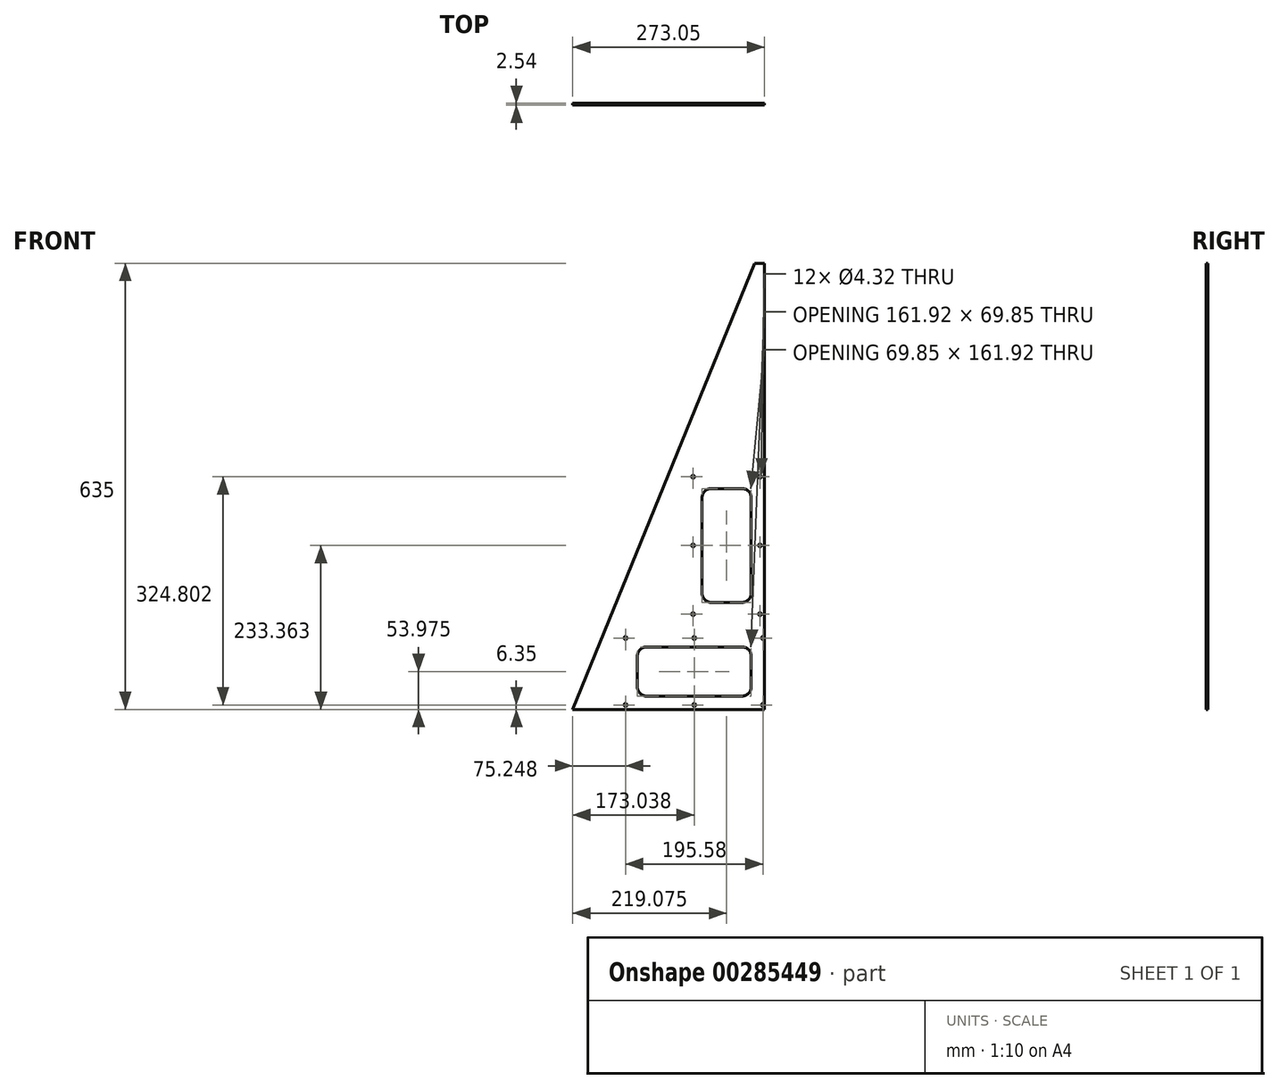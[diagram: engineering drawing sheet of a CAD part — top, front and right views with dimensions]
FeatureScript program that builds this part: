
annotation { "Feature Type Name" : "Feature", "Feature Type Description" : "" }
export const myFeature = defineFeature(function(context is Context, id is Id, definition is map)
    precondition{}
    {
        {
            var Q0;
            Q0=qCreatedBy(makeId("Front.planeOp"),FACE);
            var sketch = newSketch(context, id + "F0", { "sketchPlane" : qUnion([Q0])});
            skLineSegment(sketch, "E0", {"start": v(0, 0) * mm, "end": v(0, 635) * mm});
            skArc(sketch, "E1.MirrorCS", {"start": v(-88.9, 165.1) * mm, "mid": v(-85.18, 156.12) * mm, "end": v(-76.2, 152.4) * mm});
            skArc(sketch, "E2.MirrorCS", {"start": v(-76.2, 314.33) * mm, "mid": v(-85.18, 310.6) * mm, "end": v(-88.9, 301.63) * mm});
            skArc(sketch, "E3.MirrorCS", {"start": v(-180.97, 31.75) * mm, "mid": v(-177.26, 22.77) * mm, "end": v(-168.28, 19.05) * mm});
            skArc(sketch, "E4.MirrorCS", {"start": v(-19.05, 301.63) * mm, "mid": v(-22.77, 310.6) * mm, "end": v(-31.75, 314.33) * mm});
            skArc(sketch, "E5.MirrorCS", {"start": v(-31.75, 152.4) * mm, "mid": v(-22.77, 156.12) * mm, "end": v(-19.05, 165.1) * mm});
            skArc(sketch, "E6.MirrorCS", {"start": v(-19.05, 76.2) * mm, "mid": v(-22.77, 85.18) * mm, "end": v(-31.75, 88.9) * mm});
            skArc(sketch, "E7.MirrorCS", {"start": v(-168.28, 88.9) * mm, "mid": v(-177.26, 85.18) * mm, "end": v(-180.97, 76.2) * mm});
            skArc(sketch, "E8.MirrorCS", {"start": v(-31.75, 19.05) * mm, "mid": v(-22.77, 22.77) * mm, "end": v(-19.05, 31.75) * mm});
            skLineSegment(sketch, "E9.MirrorCS", {"start": v(-88.9, 165.1) * mm, "end": v(-88.9, 301.63) * mm});
            skLineSegment(sketch, "E10.MirrorCS", {"start": v(-76.2, 314.33) * mm, "end": v(-31.75, 314.33) * mm});
            skLineSegment(sketch, "E11.MirrorCS", {"start": v(-14.02, 635) * mm, "end": v(-273.05, 0) * mm});
            skLineSegment(sketch, "E12.MirrorCS", {"start": v(-168.28, 88.9) * mm, "end": v(-31.75, 88.9) * mm});
            skLineSegment(sketch, "E13.MirrorCS", {"start": v(-180.97, 76.2) * mm, "end": v(-180.97, 31.75) * mm});
            skLineSegment(sketch, "E14.MirrorCS", {"start": v(-76.2, 152.4) * mm, "end": v(-31.75, 152.4) * mm});
            skLineSegment(sketch, "E15.MirrorCS", {"start": v(-168.28, 19.05) * mm, "end": v(-31.75, 19.05) * mm});
            skLineSegment(sketch, "E16.MirrorCS", {"start": v(-19.05, 76.2) * mm, "end": v(-19.05, 31.75) * mm});
            skLineSegment(sketch, "E17.MirrorCS", {"start": v(-19.05, 165.1) * mm, "end": v(-19.05, 301.63) * mm});
            skLineSegment(sketch, "E18", {"start": v(-14.02, 635) * mm, "end": v(0, 635) * mm});
            skLineSegment(sketch, "E19", {"start": v(0, 0) * mm, "end": v(-273.05, 0) * mm});
            skSolve(sketch);
        }
        {
            var Q0;
            Q0=qSketchRegion(id+"F0",true);
            extrude(context, id + "F1", {"entities" : qUnion([Q0]), "depth" : 2.54 * mm});
        }
        {
            var Q0;
            Q0=makeQuery(id+"F1.opExtrude","CAP_FACE",FACE,{"disambiguationData":[OSD([sQuery(id+"F0.wireOp",EDGE,"E0"),sQuery(id+"F0.wireOp",EDGE,"de29adb0-a0ae-424e-9d03-0ac620758d970.MirrorCS"),sQuery(id+"F0.wireOp",EDGE,"de29adb0-a0ae-424e-9d03-0ac620758d971.MirrorCS"),sQuery(id+"F0.wireOp",EDGE,"de29adb0-a0ae-424e-9d03-0ac620758d972.MirrorCS"),sQuery(id+"F0.wireOp",EDGE,"de29adb0-a0ae-424e-9d03-0ac620758d973.MirrorCS"),sQuery(id+"F0.wireOp",EDGE,"de29adb0-a0ae-424e-9d03-0ac620758d974.MirrorCS"),sQuery(id+"F0.wireOp",EDGE,"de29adb0-a0ae-424e-9d03-0ac620758d975.MirrorCS"),sQuery(id+"F0.wireOp",EDGE,"de29adb0-a0ae-424e-9d03-0ac620758d976.MirrorCS"),sQuery(id+"F0.wireOp",EDGE,"de29adb0-a0ae-424e-9d03-0ac620758d977.MirrorCS"),sQuery(id+"F0.wireOp",EDGE,"de29adb0-a0ae-424e-9d03-0ac620758d978.MirrorCS"),sQuery(id+"F0.wireOp",EDGE,"de29adb0-a0ae-424e-9d03-0ac620758d979.MirrorCS"),sQuery(id+"F0.wireOp",EDGE,"de29adb0-a0ae-424e-9d03-0ac620758d9711.MirrorCS"),sQuery(id+"F0.wireOp",EDGE,"de29adb0-a0ae-424e-9d03-0ac620758d9715.MirrorCS"),sQuery(id+"F0.wireOp",EDGE,"de29adb0-a0ae-424e-9d03-0ac620758d9716.MirrorCS"),sQuery(id+"F0.wireOp",EDGE,"de29adb0-a0ae-424e-9d03-0ac620758d9717.MirrorCS"),sQuery(id+"F0.wireOp",EDGE,"de29adb0-a0ae-424e-9d03-0ac620758d9718.MirrorCS"),sQuery(id+"F0.wireOp",EDGE,"de29adb0-a0ae-424e-9d03-0ac620758d9719.MirrorCS"),sQuery(id+"F0.wireOp",EDGE,"de29adb0-a0ae-424e-9d03-0ac620758d9721.MirrorCS"),sQuery(id+"F0.wireOp",EDGE,"de29adb0-a0ae-424e-9d03-0ac620758d9723.MirrorCS"),sQuery(id+"F0.wireOp",EDGE,"de29adb0-a0ae-424e-9d03-0ac620758d9725.MirrorCS")])],"isStart":false});
            var sketch = newSketch(context, id + "F2", { "sketchPlane" : qUnion([Q0])});
            skPoint(sketch, "E20", {"position": v(-197.8, 101.6) * mm});
            skPoint(sketch, "E21", {"position": v(-100.01, 101.6) * mm});
            skPoint(sketch, "E22", {"position": v(-2.22, 101.6) * mm});
            skPoint(sketch, "E23", {"position": v(-2.22, 6.35) * mm});
            skPoint(sketch, "E24", {"position": v(-100.01, 6.35) * mm});
            skPoint(sketch, "E25", {"position": v(-197.8, 6.35) * mm});
            skLineSegment(sketch, "E26", {"start": v(-100.01, 88.9) * mm, "end": v(-100.01, 6.35) * mm, "construction": true});
            skPoint(sketch, "E27", {"position": v(-101.6, 135.57) * mm});
            skPoint(sketch, "E28", {"position": v(-101.6, 233.36) * mm});
            skPoint(sketch, "E29", {"position": v(-101.6, 331.15) * mm});
            skPoint(sketch, "E30", {"position": v(-6.35, 331.15) * mm});
            skPoint(sketch, "E31", {"position": v(-6.35, 233.36) * mm});
            skPoint(sketch, "E32", {"position": v(-6.35, 135.57) * mm});
            skLineSegment(sketch, "E33", {"start": v(-88.9, 233.36) * mm, "end": v(-6.35, 233.36) * mm, "construction": true});
            skPoint(sketch, "E33.endSnap0", {"position": v(-19.05, 233.36) * mm});
            skSolve(sketch);
        }
        {
            var Q0;
            Q0=sQuery(id+"F2.wireOp",VERTEX,"E29");
            var Q1;
            Q1=sQuery(id+"F2.wireOp",VERTEX,"E30");
            var Q2;
            Q2=sQuery(id+"F2.wireOp",VERTEX,"E31");
            var Q3;
            Q3=sQuery(id+"F2.wireOp",VERTEX,"E28");
            var Q4;
            Q4=sQuery(id+"F2.wireOp",VERTEX,"E27");
            var Q5;
            Q5=sQuery(id+"F2.wireOp",VERTEX,"E32");
            var Q6;
            Q6=sQuery(id+"F2.wireOp",VERTEX,"E20");
            var Q7;
            Q7=sQuery(id+"F2.wireOp",VERTEX,"E25");
            var Q8;
            Q8=sQuery(id+"F2.wireOp",VERTEX,"E24");
            var Q9;
            Q9=sQuery(id+"F2.wireOp",VERTEX,"E21");
            var Q10;
            Q10=sQuery(id+"F2.wireOp",VERTEX,"E22");
            var Q11;
            Q11=sQuery(id+"F2.wireOp",VERTEX,"E23");
            var Q12;
            Q12=makeQuery(id+"F1.opExtrude","SWEPT_BODY",BODY,{"disambiguationData":[OSD([sQuery(id+"F0.wireOp",EDGE,"E0"),sQuery(id+"F0.wireOp",EDGE,"de29adb0-a0ae-424e-9d03-0ac620758d970.MirrorCS"),sQuery(id+"F0.wireOp",EDGE,"de29adb0-a0ae-424e-9d03-0ac620758d971.MirrorCS"),sQuery(id+"F0.wireOp",EDGE,"de29adb0-a0ae-424e-9d03-0ac620758d972.MirrorCS"),sQuery(id+"F0.wireOp",EDGE,"de29adb0-a0ae-424e-9d03-0ac620758d973.MirrorCS"),sQuery(id+"F0.wireOp",EDGE,"de29adb0-a0ae-424e-9d03-0ac620758d974.MirrorCS"),sQuery(id+"F0.wireOp",EDGE,"de29adb0-a0ae-424e-9d03-0ac620758d975.MirrorCS"),sQuery(id+"F0.wireOp",EDGE,"de29adb0-a0ae-424e-9d03-0ac620758d976.MirrorCS"),sQuery(id+"F0.wireOp",EDGE,"de29adb0-a0ae-424e-9d03-0ac620758d977.MirrorCS"),sQuery(id+"F0.wireOp",EDGE,"de29adb0-a0ae-424e-9d03-0ac620758d978.MirrorCS"),sQuery(id+"F0.wireOp",EDGE,"de29adb0-a0ae-424e-9d03-0ac620758d979.MirrorCS"),sQuery(id+"F0.wireOp",EDGE,"de29adb0-a0ae-424e-9d03-0ac620758d9711.MirrorCS"),sQuery(id+"F0.wireOp",EDGE,"de29adb0-a0ae-424e-9d03-0ac620758d9715.MirrorCS"),sQuery(id+"F0.wireOp",EDGE,"de29adb0-a0ae-424e-9d03-0ac620758d9716.MirrorCS"),sQuery(id+"F0.wireOp",EDGE,"de29adb0-a0ae-424e-9d03-0ac620758d9717.MirrorCS"),sQuery(id+"F0.wireOp",EDGE,"de29adb0-a0ae-424e-9d03-0ac620758d9718.MirrorCS"),sQuery(id+"F0.wireOp",EDGE,"de29adb0-a0ae-424e-9d03-0ac620758d9719.MirrorCS"),sQuery(id+"F0.wireOp",EDGE,"de29adb0-a0ae-424e-9d03-0ac620758d9721.MirrorCS"),sQuery(id+"F0.wireOp",EDGE,"de29adb0-a0ae-424e-9d03-0ac620758d9723.MirrorCS"),sQuery(id+"F0.wireOp",EDGE,"de29adb0-a0ae-424e-9d03-0ac620758d9725.MirrorCS")])]});
            hole(context, id + "F3", {"style" : HoleStyle.SIMPLE, "endStyle" : HoleEndStyle.THROUGH, "standardTappedOrClearance" : lookupTablePath({ "standard" : "ANSI", "fit" : "Close", "size" : "#8", "type" : "Clearance" }), "standardBlindInLast" : lookupTablePath({ "fit" : "Close", "standard" : "ANSI", "size" : "#8", "type" : "Clearance" }), "holeDiameter" : 4.32 * mm, "isTappedThrough" : true, "tappedDepth" : 2.4 * mm, "tapClearance" : 3, "startFromSketch" : true, "locations" : qUnion([Q0, Q1, Q2, Q3, Q4, Q5, Q6, Q7, Q8, Q9, Q10, Q11]), "scope" : qUnion([Q12])});
        }
    });
